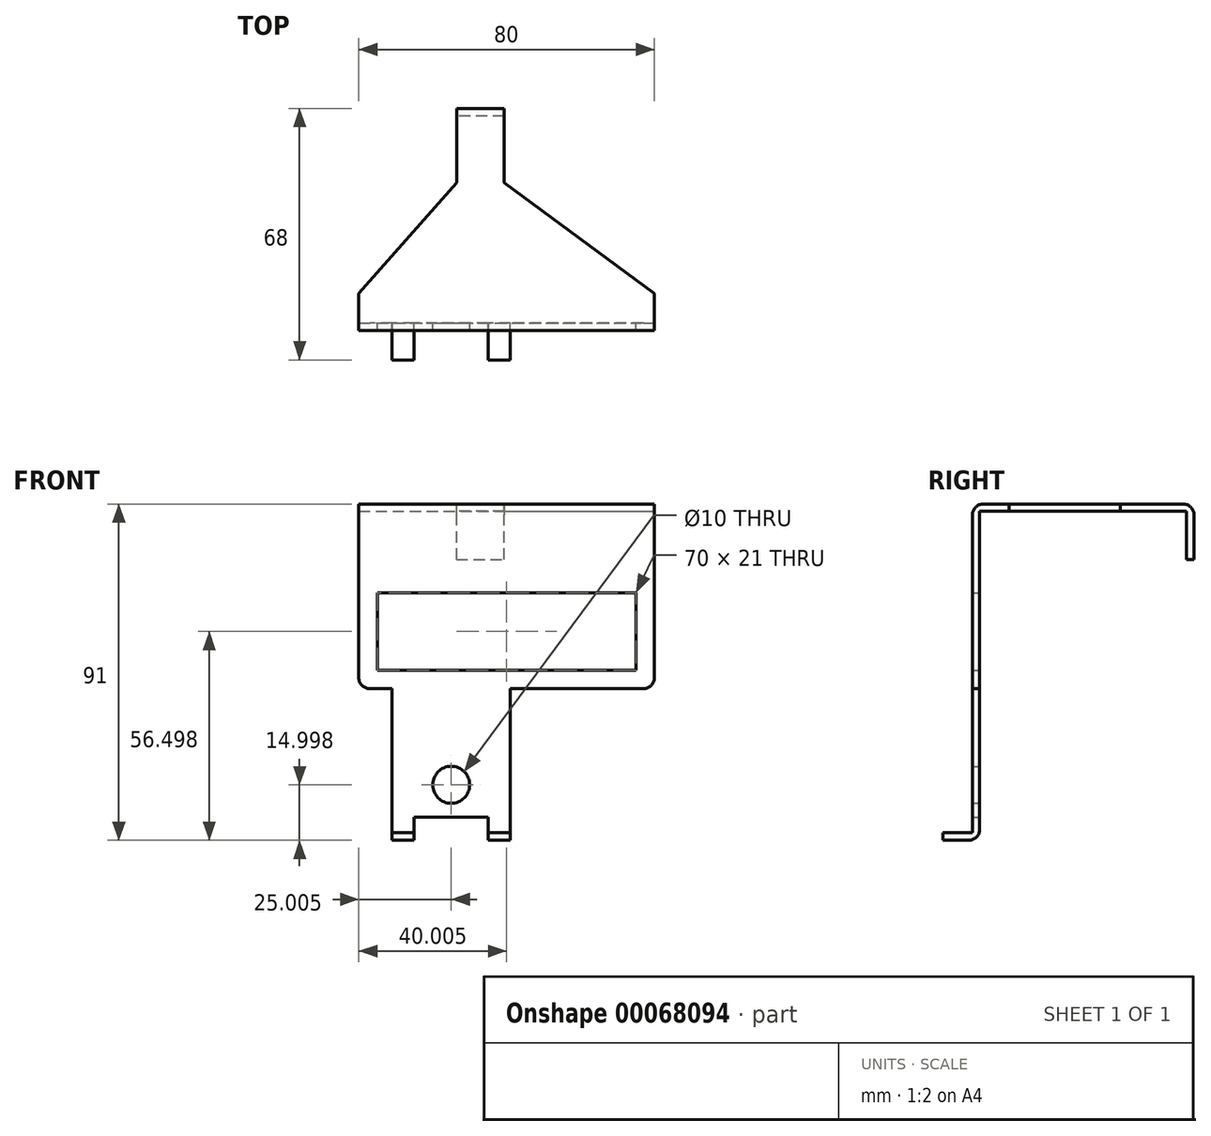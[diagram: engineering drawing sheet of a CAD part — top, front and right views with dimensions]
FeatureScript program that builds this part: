
annotation { "Feature Type Name" : "Feature", "Feature Type Description" : "" }
export const myFeature = defineFeature(function(context is Context, id is Id, definition is map)
    precondition{}
    {
        {
            var Q0;
            Q0=qCreatedBy(makeId("Front.planeOp"),FACE);
            var sketch = newSketch(context, id + "F0", { "sketchPlane" : qUnion([Q0])});
            skLineSegment(sketch, "E0", {"start": v(-51.04, 43.88) * mm, "end": v(28.96, 43.88) * mm});
            skLineSegment(sketch, "E1", {"start": v(28.96, 43.88) * mm, "end": v(28.96, -3.12) * mm});
            skLineSegment(sketch, "E2", {"start": v(25.96, -6.12) * mm, "end": v(-10.04, -6.12) * mm});
            skLineSegment(sketch, "E3", {"start": v(-10.04, -6.12) * mm, "end": v(-10.04, -47.12) * mm});
            skLineSegment(sketch, "E4", {"start": v(-10.04, -47.12) * mm, "end": v(-16.04, -47.12) * mm});
            skLineSegment(sketch, "E5", {"start": v(-16.04, -47.12) * mm, "end": v(-16.04, -40.87) * mm});
            skLineSegment(sketch, "E6", {"start": v(-16.04, -40.87) * mm, "end": v(-36.04, -40.87) * mm});
            skLineSegment(sketch, "E7", {"start": v(-36.04, -40.87) * mm, "end": v(-36.04, -47.12) * mm});
            skLineSegment(sketch, "E8", {"start": v(-36.04, -47.12) * mm, "end": v(-42.04, -47.12) * mm});
            skLineSegment(sketch, "E9", {"start": v(-42.04, -47.12) * mm, "end": v(-42.04, -6.12) * mm});
            skLineSegment(sketch, "E10", {"start": v(-42.04, -6.12) * mm, "end": v(-48.04, -6.12) * mm});
            skLineSegment(sketch, "E11", {"start": v(-51.04, -3.12) * mm, "end": v(-51.04, 43.88) * mm});
            skLineSegment(sketch, "E12.bottom", {"start": v(-46.04, 19.88) * mm, "end": v(23.96, 19.88) * mm});
            skLineSegment(sketch, "E12.top", {"start": v(-46.04, -1.12) * mm, "end": v(23.96, -1.12) * mm});
            skLineSegment(sketch, "E12.left", {"start": v(-46.04, 19.88) * mm, "end": v(-46.04, -1.12) * mm});
            skLineSegment(sketch, "E12.right", {"start": v(23.96, 19.88) * mm, "end": v(23.96, -1.12) * mm});
            skCircle(sketch, "E13", {"center": v(-26.04, -32.12) * mm, "radius": 5 * mm});
            skPoint(sketch, "E14.visualSharp", {"position": v(-51.04, -6.12) * mm});
            skArc(sketch, "E14.filletArc", {"start": v(-51.04, -3.12) * mm, "mid": v(-50.16, -5.24) * mm, "end": v(-48.04, -6.12) * mm});
            skPoint(sketch, "E15.visualSharp", {"position": v(28.96, -6.12) * mm});
            skArc(sketch, "E15.filletArc", {"start": v(25.96, -6.12) * mm, "mid": v(28.09, -5.24) * mm, "end": v(28.96, -3.12) * mm});
            skSolve(sketch);
        }
        {
            var Q0;
            Q0=makeQuery(id+"F0.imprint","IMPRINT",FACE,{"disambiguationData":[TD([[makeQuery(id+"F0.imprint","IMPRINT",EDGE,{"derivedFrom":sQuery(id+"F0.wireOp",EDGE,"E0")}),-1.0]])]});
            extrude(context, id + "F1", {"entities" : qUnion([Q0]), "depth" : 2 * mm});
        }
        {
            var Q0;
            Q0=makeQuery(id+"F1.opExtrude","CAP_FACE",FACE,{"disambiguationData":[OSD([sQuery(id+"F0.wireOp",EDGE,"E0"),sQuery(id+"F0.wireOp",EDGE,"E1"),sQuery(id+"F0.wireOp",EDGE,"E2"),sQuery(id+"F0.wireOp",EDGE,"E3"),sQuery(id+"F0.wireOp",EDGE,"E4"),sQuery(id+"F0.wireOp",EDGE,"E5"),sQuery(id+"F0.wireOp",EDGE,"E6"),sQuery(id+"F0.wireOp",EDGE,"E7"),sQuery(id+"F0.wireOp",EDGE,"E8"),sQuery(id+"F0.wireOp",EDGE,"E9"),sQuery(id+"F0.wireOp",EDGE,"E10"),sQuery(id+"F0.wireOp",EDGE,"E11"),sQuery(id+"F0.wireOp",EDGE,"E12.bottom"),sQuery(id+"F0.wireOp",EDGE,"E12.top"),sQuery(id+"F0.wireOp",EDGE,"E12.left"),sQuery(id+"F0.wireOp",EDGE,"E12.right"),sQuery(id+"F0.wireOp",EDGE,"E13"),sQuery(id+"F0.wireOp",EDGE,"E14.filletArc"),sQuery(id+"F0.wireOp",EDGE,"E15.filletArc")])],"isStart":false});
            var sketch = newSketch(context, id + "F2", { "sketchPlane" : qUnion([Q0])});
            skLineSegment(sketch, "E16.bottom", {"start": v(-42.04, -47.12) * mm, "end": v(-36.04, -47.12) * mm});
            skLineSegment(sketch, "E16.top", {"start": v(-42.04, -45.12) * mm, "end": v(-36.04, -45.12) * mm});
            skLineSegment(sketch, "E16.left", {"start": v(-42.04, -47.12) * mm, "end": v(-42.04, -45.12) * mm});
            skLineSegment(sketch, "E16.right", {"start": v(-36.04, -47.12) * mm, "end": v(-36.04, -45.12) * mm});
            skLineSegment(sketch, "E17.bottom", {"start": v(-16.04, -45.12) * mm, "end": v(-10.04, -45.12) * mm});
            skLineSegment(sketch, "E17.top", {"start": v(-16.04, -47.12) * mm, "end": v(-10.04, -47.12) * mm});
            skLineSegment(sketch, "E17.left", {"start": v(-16.04, -45.12) * mm, "end": v(-16.04, -47.12) * mm});
            skLineSegment(sketch, "E17.right", {"start": v(-10.04, -45.12) * mm, "end": v(-10.04, -47.12) * mm});
            skSolve(sketch);
        }
        {
            var Q0;
            Q0=makeQuery(id+"F2.imprint","IMPRINT",FACE,{"disambiguationData":[TD([[makeQuery(id+"F2.imprint","IMPRINT",EDGE,{"derivedFrom":sQuery(id+"F2.wireOp",EDGE,"E16.bottom")}),-1.0]])]});
            var Q1;
            Q1=makeQuery(id+"F2.imprint","IMPRINT",FACE,{"disambiguationData":[TD([[makeQuery(id+"F2.imprint","IMPRINT",EDGE,{"derivedFrom":sQuery(id+"F2.wireOp",EDGE,"E17.bottom")}),-1.0]])]});
            extrude(context, id + "F3", {"entities" : qUnion([Q0, Q1]), "operationType" : NewBodyOperationType.ADD, "depth" : 8 * mm});
        }
        {
            var Q0;
            Q0=makeQuery(id+"F1.opExtrude","CAP_EDGE",EDGE,{"disambiguationData":[OSD([sQuery(id+"F0.wireOp",EDGE,"E4")])],"isStart":true});
            var Q1;
            Q1=makeQuery(id+"F1.opExtrude","CAP_EDGE",EDGE,{"disambiguationData":[OSD([sQuery(id+"F0.wireOp",EDGE,"E8")])],"isStart":true});
            fillet(context, id + "F4", {"entities" : qUnion([Q0, Q1]), "radius" : 3 * mm, "tangentPropagation" : true, "allowEdgeOverflow" : false});
        }
        {
            var Q0;
            Q0=makeQuery(id+"F1.opExtrude","SWEPT_FACE",FACE,{"disambiguationData":[OSD([sQuery(id+"F0.wireOp",EDGE,"E0")])]});
            var sketch = newSketch(context, id + "F5", { "sketchPlane" : qUnion([Q0])});
            skLineSegment(sketch, "E18", {"start": v(-51.04, -2) * mm, "end": v(-51.04, 8) * mm});
            skLineSegment(sketch, "E19", {"start": v(-51.04, 8) * mm, "end": v(-24.56, 38) * mm});
            skLineSegment(sketch, "E20", {"start": v(-24.56, 38) * mm, "end": v(-24.56, 58) * mm});
            skLineSegment(sketch, "E21", {"start": v(-24.56, 58) * mm, "end": v(-11.71, 58) * mm});
            skLineSegment(sketch, "E22", {"start": v(-11.71, 58) * mm, "end": v(-11.71, 38) * mm});
            skLineSegment(sketch, "E23", {"start": v(-11.71, 38) * mm, "end": v(28.96, 8) * mm});
            skLineSegment(sketch, "E24", {"start": v(28.96, 8) * mm, "end": v(28.96, -2) * mm});
            skLineSegment(sketch, "E25", {"start": v(28.96, -2) * mm, "end": v(-51.04, -2) * mm});
            skSolve(sketch);
        }
        {
            var Q0;
            {var subQ1=sQuery(id+"F5.wireOp",EDGE,"E19");Q0=makeQuery(id+"F5.imprint","IMPRINT",FACE,{"disambiguationData":[TD([[makeQuery(id+"F5.imprint","IMPRINT",EDGE,{"derivedFrom":subQ1}),-1.0]])]});}
            extrude(context, id + "F6", {"entities" : qUnion([Q0]), "operationType" : NewBodyOperationType.ADD, "oppositeDirection" : true, "depth" : 2 * mm});
        }
        {
            var Q0;
            Q0=makeQuery(id+"F6.opExtrude","CAP_FACE",FACE,{"disambiguationData":[OSD([sQuery(id+"F0.wireOp",EDGE,"E0"),sQuery(id+"F5.wireOp",EDGE,"E18"),sQuery(id+"F5.wireOp",EDGE,"E19"),sQuery(id+"F5.wireOp",EDGE,"E20"),sQuery(id+"F5.wireOp",EDGE,"E21"),sQuery(id+"F5.wireOp",EDGE,"E22"),sQuery(id+"F5.wireOp",EDGE,"E23"),sQuery(id+"F5.wireOp",EDGE,"E24")])],"isStart":false});
            var sketch = newSketch(context, id + "F7", { "sketchPlane" : qUnion([Q0])});
            skLineSegment(sketch, "E26.bottom", {"start": v(-11.71, -58) * mm, "end": v(-24.56, -58) * mm});
            skLineSegment(sketch, "E26.top", {"start": v(-11.71, -56) * mm, "end": v(-24.56, -56) * mm});
            skLineSegment(sketch, "E26.left", {"start": v(-11.71, -58) * mm, "end": v(-11.71, -56) * mm});
            skLineSegment(sketch, "E26.right", {"start": v(-24.56, -58) * mm, "end": v(-24.56, -56) * mm});
            skSolve(sketch);
        }
        {
            var Q0;
            Q0=makeQuery(id+"F7.imprint","IMPRINT",FACE,{"disambiguationData":[TD([[makeQuery(id+"F7.imprint","IMPRINT",EDGE,{"derivedFrom":sQuery(id+"F7.wireOp",EDGE,"E26.bottom")}),1.0]])]});
            extrude(context, id + "F8", {"entities" : qUnion([Q0]), "operationType" : NewBodyOperationType.ADD, "depth" : 13 * mm});
        }
        {
            var Q0;
            Q0=makeQuery(id+"F6.opExtrude","CAP_EDGE",EDGE,{"disambiguationData":[OSD([sQuery(id+"F5.wireOp",EDGE,"E21")])],"isStart":true});
            var Q1;
            Q1=makeQuery(id+"F1.opExtrude","CAP_EDGE",EDGE,{"disambiguationData":[OSD([sQuery(id+"F0.wireOp",EDGE,"E0")])],"isStart":false});
            fillet(context, id + "F9", {"entities" : qUnion([Q0, Q1]), "radius" : 3 * mm, "tangentPropagation" : true, "allowEdgeOverflow" : false});
        }
    });
